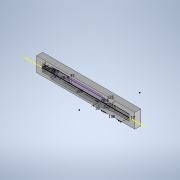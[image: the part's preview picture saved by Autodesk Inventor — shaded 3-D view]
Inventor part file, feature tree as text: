
AUTODESK INVENTOR PART (.ipt)
format: ipt  version: 2022 (Build 260153000, 153)  size: 236,032 bytes
history: native  units: mm
features: sketch x2, extrude x2, revolve x1, fillet x1, boolean_combine x1
ambient origin geometry x8: Origin, YZ Plane, XZ Plane, XY Plane, X Axis, Y Axis, Z Axis, Center Point
bodies: Solid2 (feature_tree), Solid3 (feature_tree)
feature tree (7):
  sketch  "Sketch1"  dims[d0=41.0mm d1=6.0mm]
  revolve  "Revolution2"  [1 undecoded]
  extrude  "Extrusion2"  Depth=200.0mm
  fillet  "Fillet1"  Radius=50.0mm
  extrude  "Extrusion3"  Depth=100.0mm
  boolean_combine  "Combine1"
  sketch  "Sketch2"  dims[d2=59.0mm d3=200.0mm d4=50.0mm d5=100.0mm d6=19.5mm d7=19.5mm d8=28.5mm d10=28.5mm d11=17.0mm d12=17.0mm d13=2.0mm d14=8.0mm d16=125.0mm d17=125.0mm d18=2.0mm d25=35.0mm d26=28.5mm d27=180.0deg d28=100.0mm d29=0.0mm d30=2.0mm d31=516.0mm d32=77.0mm d33=31.5mm d34=0.0mm d19=0.872665mm d20=0.872665mm]
note: 1 required parameter value undecoded (feature->parameter linkage not recoverable at this tier; creation-order binding heuristic only, values carry confidence <= 0.55)
